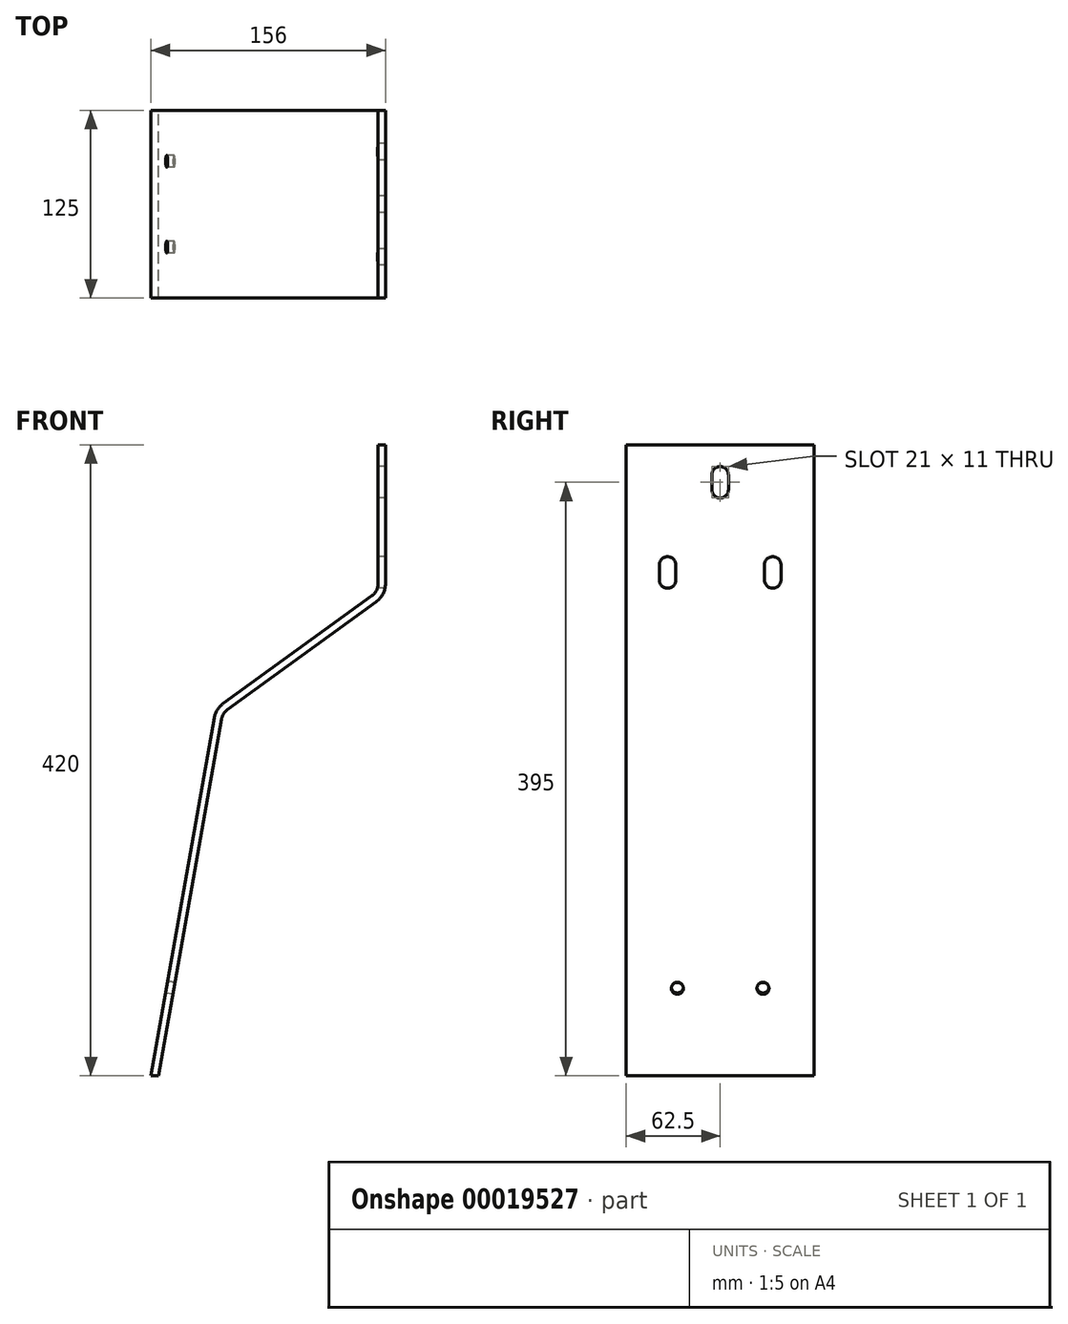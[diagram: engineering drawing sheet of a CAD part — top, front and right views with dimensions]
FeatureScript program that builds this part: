
annotation { "Feature Type Name" : "Feature", "Feature Type Description" : "" }
export const myFeature = defineFeature(function(context is Context, id is Id, definition is map)
    precondition{}
    {
        {
            var Q0;
            Q0=qCreatedBy(makeId("Front.planeOp"),FACE);
            var sketch = newSketch(context, id + "F0", { "sketchPlane" : qUnion([Q0])});
            skLineSegment(sketch, "E0", {"start": v(0, 0) * mm, "end": v(42.54, 241.28) * mm});
            skLineSegment(sketch, "E1", {"start": v(42.54, 241.28) * mm, "end": v(151, 320) * mm});
            skLineSegment(sketch, "E2", {"start": v(151, 320) * mm, "end": v(151, 420) * mm});
            skLineSegment(sketch, "E3", {"start": v(0, 0) * mm, "end": v(5, 0) * mm});
            skLineSegment(sketch, "E4", {"start": v(5, 0) * mm, "end": v(40.03, 198.68) * mm, "construction": true});
            skArc(sketch, "E5", {"start": v(89.27, 240) * mm, "mid": v(57.13, 228.3) * mm, "end": v(40.03, 198.68) * mm, "construction": true});
            skLineSegment(sketch, "E6", {"start": v(89.27, 240) * mm, "end": v(418.34, 240) * mm, "construction": true});
            skLineSegment(sketch, "E7", {"start": v(161.93, 335) * mm, "end": v(298.2, 335) * mm, "construction": true});
            skLineSegment(sketch, "E8", {"start": v(412.6, 255) * mm, "end": v(198.91, 255) * mm, "construction": true});
            skLineSegment(sketch, "E9.0", {"start": v(146.08, 322.51) * mm, "end": v(146.08, 420) * mm});
            skLineSegment(sketch, "E9.1", {"start": v(38.04, 244.1) * mm, "end": v(146.08, 322.51) * mm});
            skLineSegment(sketch, "E9.2", {"start": v(-5, 0) * mm, "end": v(38.04, 244.1) * mm});
            skLineSegment(sketch, "E10", {"start": v(151, 420) * mm, "end": v(146.08, 420) * mm});
            skLineSegment(sketch, "E11", {"start": v(0, 0) * mm, "end": v(-5, 0) * mm});
            skLineSegment(sketch, "E12", {"start": v(5, 0) * mm, "end": v(5, -158.08) * mm, "construction": true});
            skSolve(sketch);
        }
        {
            var Q0;
            Q0 = qSketchRegion(id + "F0", true);
            extrude(context, id + "F1", {"entities" : qUnion([Q0]), "depth" : 125 * mm});
        }
        {
            var Q0;
            Q0=makeQuery(id+"F1.opExtrude","SWEPT_EDGE",EDGE,{"disambiguationData":[OSD([sQuery(id+"F0.wireOp",EDGE,"E9.0"),sQuery(id+"F0.wireOp",EDGE,"E9.1")])]});
            var Q1;
            Q1=makeQuery(id+"F1.opExtrude","SWEPT_EDGE",EDGE,{"disambiguationData":[OSD([sQuery(id+"F0.wireOp",EDGE,"E0"),sQuery(id+"F0.wireOp",EDGE,"E1")])]});
            fillet(context, id + "F2", {"entities" : qUnion([Q0, Q1]), "radius" : 10 * mm, "tangentPropagation" : true, "allowEdgeOverflow" : false});
        }
        {
            var Q0;
            Q0=makeQuery(id+"F1.opExtrude","SWEPT_EDGE",EDGE,{"disambiguationData":[OSD([sQuery(id+"F0.wireOp",EDGE,"E1"),sQuery(id+"F0.wireOp",EDGE,"E2")])]});
            var Q1;
            Q1=makeQuery(id+"F1.opExtrude","SWEPT_EDGE",EDGE,{"disambiguationData":[OSD([sQuery(id+"F0.wireOp",EDGE,"E9.1"),sQuery(id+"F0.wireOp",EDGE,"E9.2")])]});
            fillet(context, id + "F3", {"entities" : qUnion([Q0, Q1]), "radius" : 15 * mm, "tangentPropagation" : true, "allowEdgeOverflow" : false});
        }
        {
            var Q0;
            Q0=makeQuery(id+"F1.opExtrude","SWEPT_FACE",FACE,{"disambiguationData":[OSD([sQuery(id+"F0.wireOp",EDGE,"E9.0")])]});
            var sketch = newSketch(context, id + "F4", { "sketchPlane" : qUnion([Q0])});
            skLineSegment(sketch, "E13", {"start": v(-40.1, 335) * mm, "end": v(192.9, 335) * mm, "construction": true});
            skLineSegment(sketch, "E14", {"start": v(-63.95, 395) * mm, "end": v(170.68, 395) * mm, "construction": true});
            skLineSegment(sketch, "E15", {"start": v(97.5, 400.75) * mm, "end": v(97.5, 327.6) * mm, "construction": true});
            skLineSegment(sketch, "E16", {"start": v(27.5, 401.69) * mm, "end": v(27.5, 335) * mm, "construction": true});
            skArc(sketch, "E17", {"start": v(103, 340) * mm, "mid": v(97.5, 345.5) * mm, "end": v(92, 340) * mm});
            skLineSegment(sketch, "E18", {"start": v(92, 340) * mm, "end": v(92, 330) * mm});
            skLineSegment(sketch, "E19", {"start": v(103, 340) * mm, "end": v(103, 330) * mm});
            skArc(sketch, "E20", {"start": v(92, 330) * mm, "mid": v(97.5, 324.5) * mm, "end": v(103, 330) * mm});
            skArc(sketch, "E21", {"start": v(22, 330) * mm, "mid": v(27.5, 324.5) * mm, "end": v(33, 330) * mm});
            skLineSegment(sketch, "E22", {"start": v(33, 340) * mm, "end": v(33, 330) * mm});
            skLineSegment(sketch, "E23", {"start": v(22, 340) * mm, "end": v(22, 330) * mm});
            skArc(sketch, "E24", {"start": v(33, 340) * mm, "mid": v(27.5, 345.5) * mm, "end": v(22, 340) * mm});
            skArc(sketch, "E25", {"start": v(57, 390) * mm, "mid": v(62.5, 384.5) * mm, "end": v(68, 390) * mm});
            skLineSegment(sketch, "E26", {"start": v(68, 400) * mm, "end": v(68, 390) * mm});
            skLineSegment(sketch, "E27", {"start": v(57, 400) * mm, "end": v(57, 390) * mm});
            skArc(sketch, "E28", {"start": v(68, 400) * mm, "mid": v(62.5, 405.5) * mm, "end": v(57, 400) * mm});
            skSolve(sketch);
        }
        {
            var Q0;
            Q0 = qSketchRegion(id + "F4", true);
            extrude(context, id + "F5", {"entities" : qUnion([Q0]), "operationType" : NewBodyOperationType.REMOVE, "endBound" : BoundingType.THROUGH_ALL, "oppositeDirection" : true, "depth" : 25 * mm, "hasSecondDirection" : true, "secondDirectionBound" : SecondDirectionBoundingType.THROUGH_ALL, "secondDirectionOppositeDirection" : false, "secondDirectionDepth" : 25 * mm});
        }
        {
            var Q0;
            Q0=makeQuery(id+"F1.opExtrude","SWEPT_FACE",FACE,{"disambiguationData":[OSD([sQuery(id+"F0.wireOp",EDGE,"E9.2")])]});
            var sketch = newSketch(context, id + "F6", { "sketchPlane" : qUnion([Q0])});
            skPoint(sketch, "E29", {"position": v(34, 59.13) * mm});
            skPoint(sketch, "E30", {"position": v(91, 59.13) * mm});
            skSolve(sketch);
        }
        {
            var Q0;
            Q0=sQuery(id+"F6.wireOp",VERTEX,"E30");
            var Q1;
            Q1=sQuery(id+"F6.wireOp",VERTEX,"E29");
            var Q2;
            Q2=makeQuery(id+"F1.opExtrude","SWEPT_BODY",BODY,{"disambiguationData":[OSD([sQuery(id+"F0.wireOp",EDGE,"E0"),sQuery(id+"F0.wireOp",EDGE,"E1"),sQuery(id+"F0.wireOp",EDGE,"E2"),sQuery(id+"F0.wireOp",EDGE,"E9.0"),sQuery(id+"F0.wireOp",EDGE,"E9.1"),sQuery(id+"F0.wireOp",EDGE,"E9.2"),sQuery(id+"F0.wireOp",EDGE,"E10"),sQuery(id+"F0.wireOp",EDGE,"E11")])]});
            hole(context, id + "F7", {"style" : HoleStyle.SIMPLE, "holeDiameter" : 8 * mm, "endStyle" : HoleEndStyle.THROUGH, "locations" : qUnion([Q0, Q1]), "scope" : qUnion([Q2])});
        }
    });
